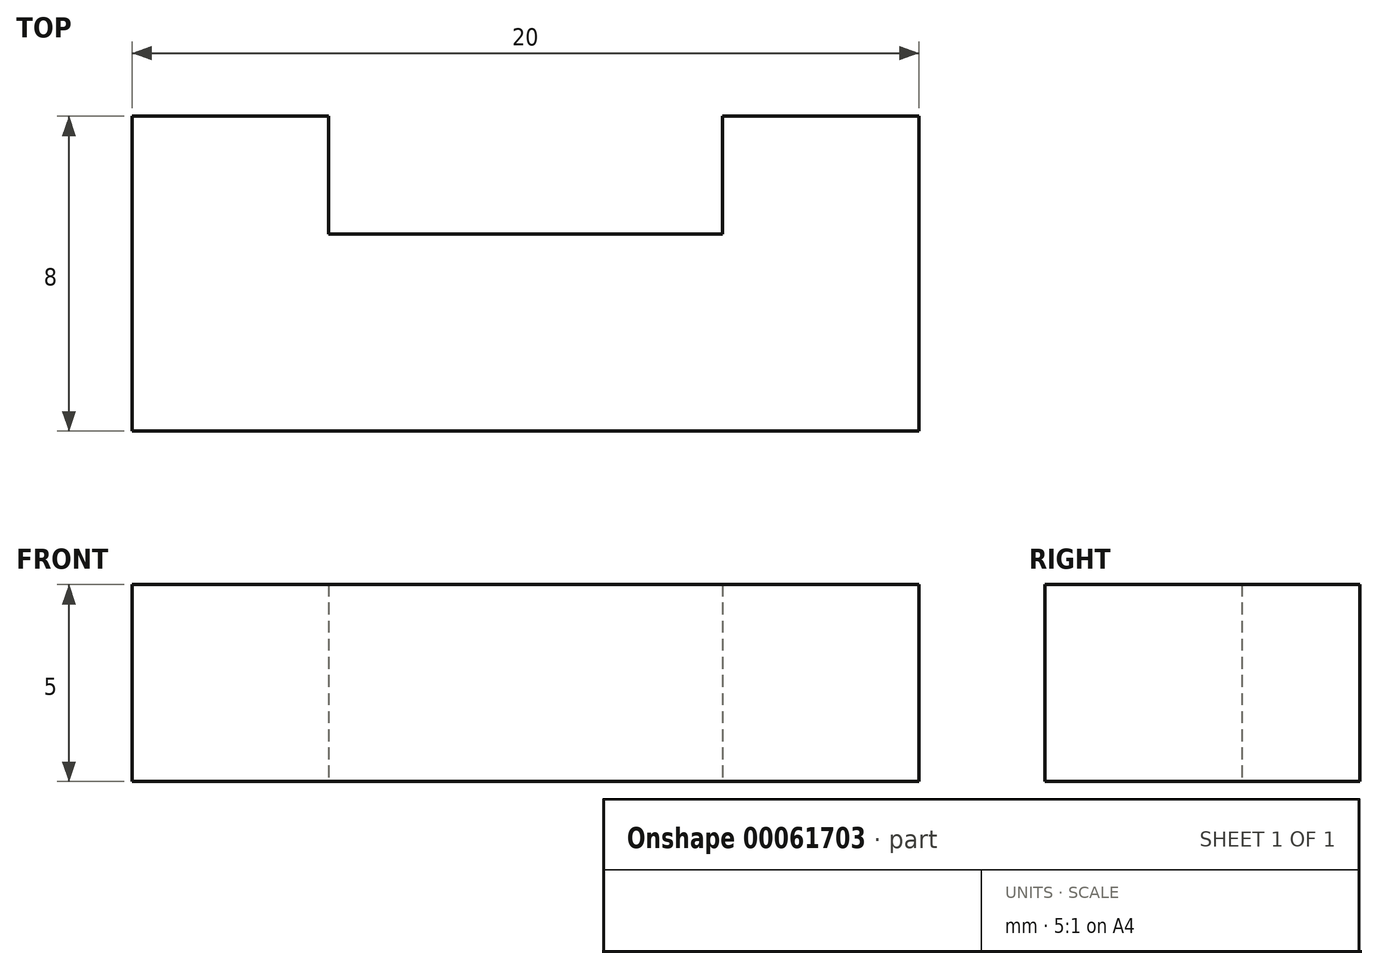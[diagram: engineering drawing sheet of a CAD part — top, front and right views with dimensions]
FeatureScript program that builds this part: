
annotation { "Feature Type Name" : "Feature", "Feature Type Description" : "" }
export const myFeature = defineFeature(function(context is Context, id is Id, definition is map)
    precondition{}
    {
        {
            var Q0;
            Q0=qCreatedBy(makeId("Top.planeOp"),FACE);
            var sketch = newSketch(context, id + "F0", { "sketchPlane" : qUnion([Q0])});
            skLineSegment(sketch, "E0", {"start": v(0, 0) * mm, "end": v(20, 0) * mm});
            skLineSegment(sketch, "E1", {"start": v(20, 0) * mm, "end": v(20, 8) * mm});
            skLineSegment(sketch, "E2", {"start": v(20, 8) * mm, "end": v(15, 8) * mm});
            skLineSegment(sketch, "E3", {"start": v(15, 8) * mm, "end": v(15, 5) * mm});
            skLineSegment(sketch, "E4", {"start": v(15, 5) * mm, "end": v(5, 5) * mm});
            skLineSegment(sketch, "E5", {"start": v(5, 5) * mm, "end": v(5, 8) * mm});
            skLineSegment(sketch, "E6", {"start": v(5, 8) * mm, "end": v(0, 8) * mm});
            skLineSegment(sketch, "E7", {"start": v(0, 8) * mm, "end": v(0, 0) * mm});
            skSolve(sketch);
        }
        {
            var Q0;
            Q0 = qSketchRegion(id + "F0", true);
            extrude(context, id + "F1", {"entities" : qUnion([Q0]), "depth" : 5 * mm});
        }
    });
